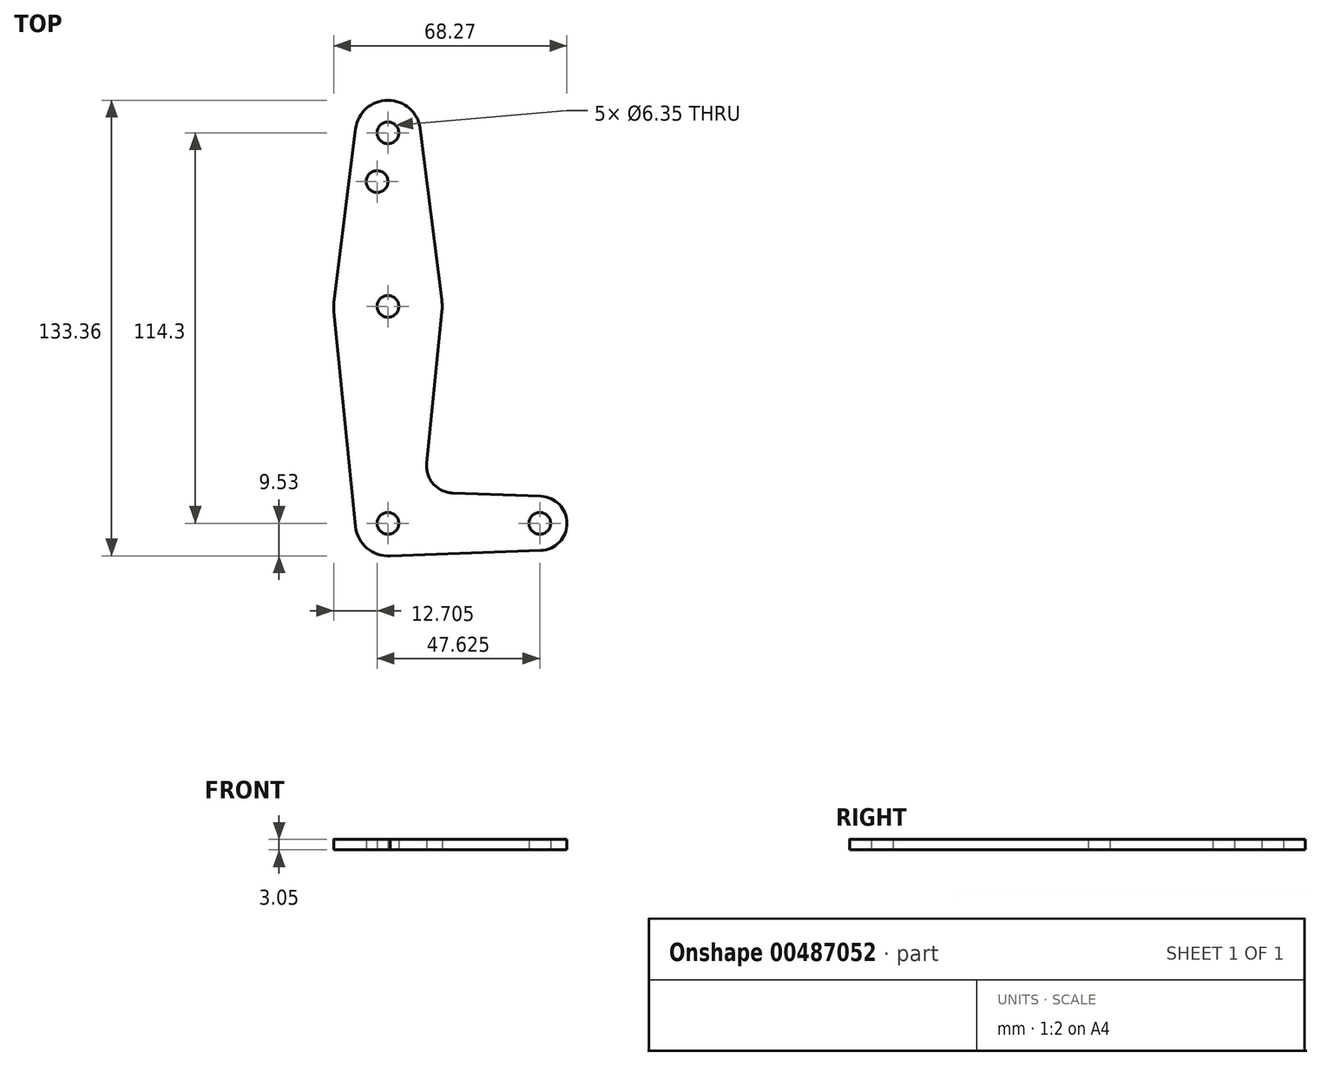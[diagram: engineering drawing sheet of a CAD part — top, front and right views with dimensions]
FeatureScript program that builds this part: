
annotation { "Feature Type Name" : "Feature", "Feature Type Description" : "" }
export const myFeature = defineFeature(function(context is Context, id is Id, definition is map)
    precondition{}
    {
        {
            var Q0;
            Q0=qCreatedBy(makeId("Top.planeOp"),FACE);
            var sketch = newSketch(context, id + "F0", { "sketchPlane" : qUnion([Q0])});
            skLineSegment(sketch, "E0", {"start": v(0, 0) * mm, "end": v(0, 114.3) * mm, "construction": true});
            skLineSegment(sketch, "E1", {"start": v(0, 0) * mm, "end": v(44.45, 0) * mm, "construction": true});
            skCircle(sketch, "E2", {"center": v(0, 0) * mm, "radius": 9.53 * mm});
            skCircle(sketch, "E3", {"center": v(0, 114.3) * mm, "radius": 9.53 * mm});
            skCircle(sketch, "E4", {"center": v(44.45, 0) * mm, "radius": 7.94 * mm});
            skCircle(sketch, "E5", {"center": v(0, 63.5) * mm, "radius": 15.88 * mm});
            skLineSegment(sketch, "E6", {"start": v(9.45, 115.5) * mm, "end": v(15.75, 65.48) * mm});
            skLineSegment(sketch, "E7", {"start": v(-9.45, 115.5) * mm, "end": v(-15.75, 65.48) * mm});
            skLineSegment(sketch, "E8", {"start": v(15.8, 61.91) * mm, "end": v(11.34, 17.6) * mm});
            skLineSegment(sketch, "E9", {"start": v(-15.8, 61.91) * mm, "end": v(-9.48, -0.95) * mm});
            skLineSegment(sketch, "E10", {"start": v(0, -9.53) * mm, "end": v(44.73, -7.93) * mm});
            skLineSegment(sketch, "E11", {"start": v(44.73, 7.93) * mm, "end": v(18.97, 8.85) * mm});
            skCircle(sketch, "E12", {"center": v(0, 114.3) * mm, "radius": 3.18 * mm});
            skCircle(sketch, "E13", {"center": v(0, 63.5) * mm, "radius": 3.18 * mm});
            skCircle(sketch, "E14", {"center": v(0, 0) * mm, "radius": 3.18 * mm});
            skCircle(sketch, "E15", {"center": v(44.45, 0) * mm, "radius": 3.18 * mm});
            skCircle(sketch, "E16", {"center": v(-3.18, 100.03) * mm, "radius": 3.18 * mm});
            skArc(sketch, "E17.filletArc", {"start": v(11.34, 17.6) * mm, "mid": v(13.26, 11.57) * mm, "end": v(18.97, 8.85) * mm});
            skSolve(sketch);
        }
        {
            var Q0;
            Q0 = qSketchRegion(id + "F0", true);
            extrude(context, id + "F1", {"entities" : qUnion([Q0]), "depth" : 3.05 * mm});
        }
    });
